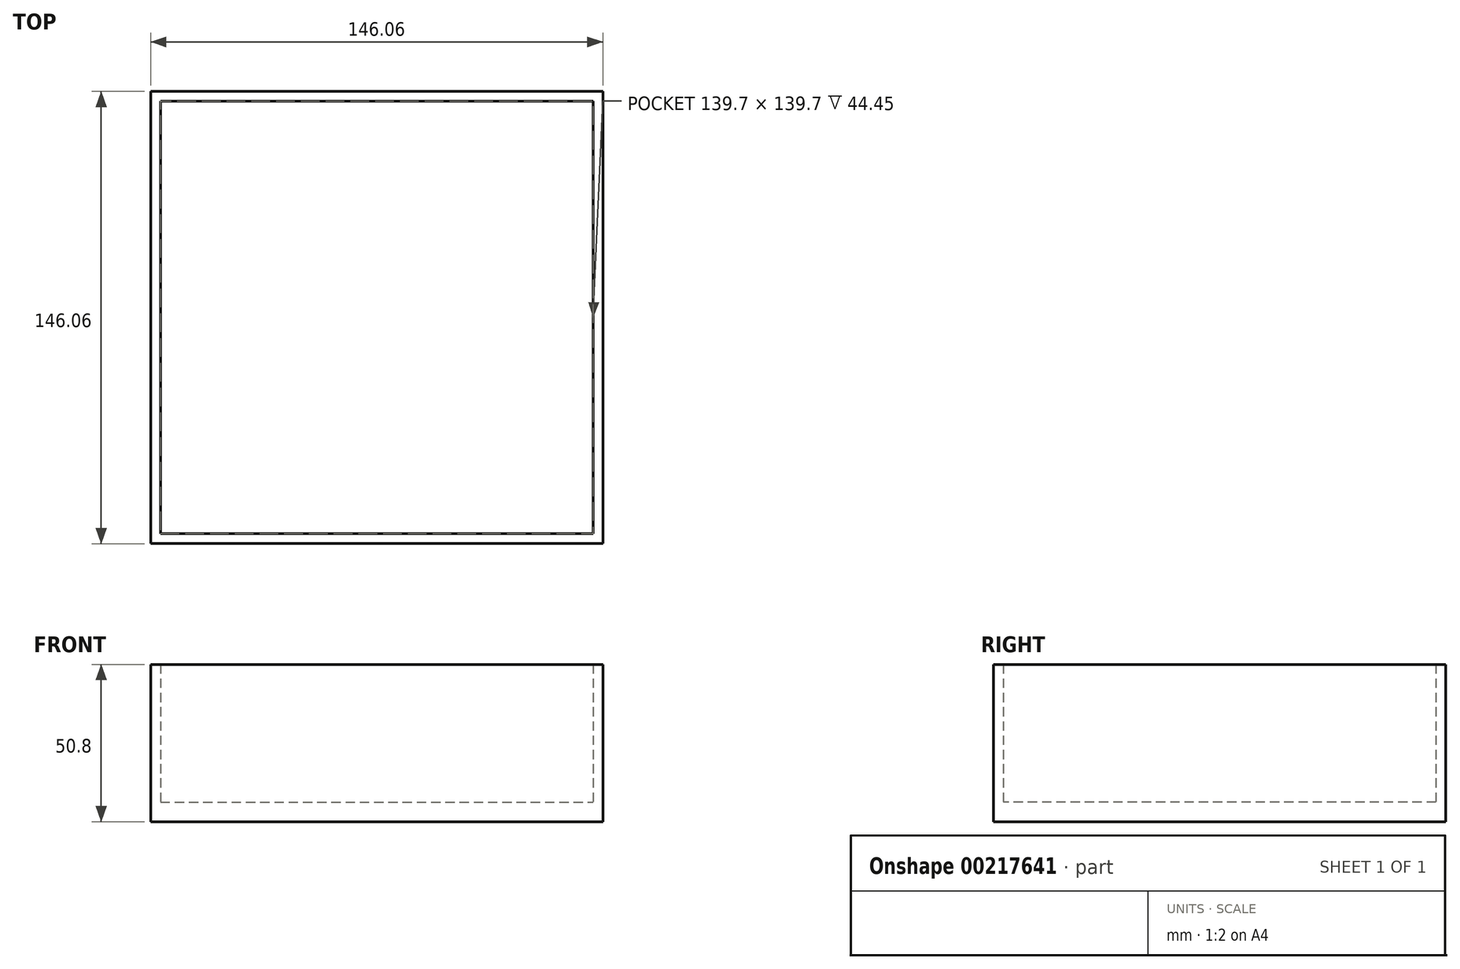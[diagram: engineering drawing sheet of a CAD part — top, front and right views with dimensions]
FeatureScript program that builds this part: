
annotation { "Feature Type Name" : "Feature", "Feature Type Description" : "" }
export const myFeature = defineFeature(function(context is Context, id is Id, definition is map)
    precondition{}
    {
        {
            var Q0;
            Q0=qCreatedBy(makeId("Top.planeOp"),FACE);
            var sketch = newSketch(context, id + "F0", { "sketchPlane" : qUnion([Q0])});
            skLineSegment(sketch, "E0.bottom", {"start": v(-67.3, 67.31) * mm, "end": v(67.31, 67.31) * mm});
            skLineSegment(sketch, "E0.top", {"start": v(-67.31, -67.31) * mm, "end": v(67.3, -67.31) * mm});
            skLineSegment(sketch, "E0.left", {"start": v(-67.3, 67.31) * mm, "end": v(-67.31, -67.31) * mm});
            skLineSegment(sketch, "E0.right", {"start": v(67.31, 67.31) * mm, "end": v(67.3, -67.31) * mm});
            skPoint(sketch, "E0.middle", {"position": v(0, 0) * mm});
            skLineSegment(sketch, "E1.bottom", {"start": v(-69.85, 69.85) * mm, "end": v(69.85, 69.85) * mm});
            skLineSegment(sketch, "E1.top", {"start": v(-69.85, -69.85) * mm, "end": v(69.85, -69.85) * mm});
            skLineSegment(sketch, "E1.left", {"start": v(-69.85, 69.85) * mm, "end": v(-69.85, -69.85) * mm});
            skLineSegment(sketch, "E1.right", {"start": v(69.85, 69.85) * mm, "end": v(69.85, -69.85) * mm});
            skLineSegment(sketch, "E2.bottom", {"start": v(-73.03, 73.03) * mm, "end": v(73.03, 73.03) * mm});
            skLineSegment(sketch, "E2.top", {"start": v(-73.03, -73.03) * mm, "end": v(73.03, -73.03) * mm});
            skLineSegment(sketch, "E2.left", {"start": v(-73.03, 73.03) * mm, "end": v(-73.03, -73.03) * mm});
            skLineSegment(sketch, "E2.right", {"start": v(73.03, 73.03) * mm, "end": v(73.03, -73.03) * mm});
            skSolve(sketch);
        }
        {
            var Q0;
            Q0=makeQuery(id+"F0.imprint","IMPRINT",FACE,{"disambiguationData":[TD([[makeQuery(id+"F0.imprint","IMPRINT",EDGE,{"derivedFrom":sQuery(id+"F0.wireOp",EDGE,"E1.bottom")}),1.0]])]});
            extrude(context, id + "F1", {"entities" : qUnion([Q0]), "depth" : 50.8 * mm});
        }
        {
            var Q0;
            Q0=makeQuery(id+"F0.imprint","IMPRINT",FACE,{"disambiguationData":[TD([[makeQuery(id+"F0.imprint","IMPRINT",EDGE,{"derivedFrom":sQuery(id+"F0.wireOp",EDGE,"E0.bottom")}),-1.0]])]});
            var Q1;
            Q1=makeQuery(id+"F0.imprint","IMPRINT",FACE,{"disambiguationData":[TD([[makeQuery(id+"F0.imprint","IMPRINT",EDGE,{"derivedFrom":sQuery(id+"F0.wireOp",EDGE,"E0.bottom")}),1.0]])]});
            extrude(context, id + "F2", {"entities" : qUnion([Q0, Q1]), "operationType" : NewBodyOperationType.ADD, "depth" : 6.35 * mm});
        }
    });
